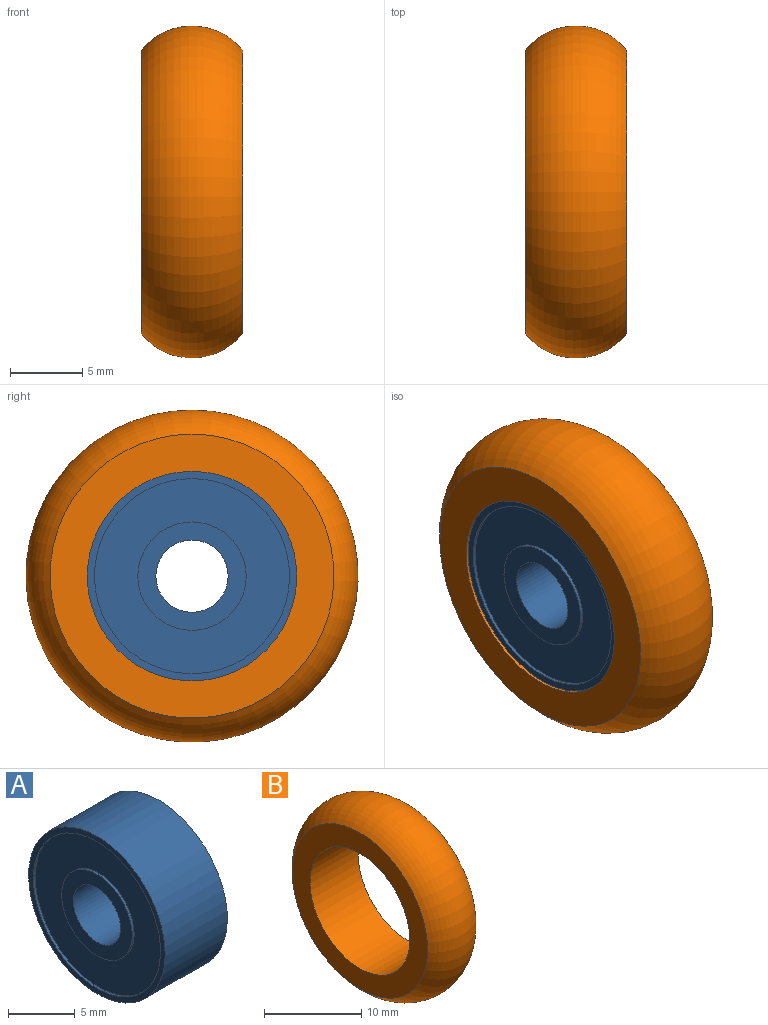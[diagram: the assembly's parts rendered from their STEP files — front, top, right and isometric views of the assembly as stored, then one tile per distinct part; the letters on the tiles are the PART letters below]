
ASSEMBLY  parts=2 mates=2
PART A: 12 faces, bbox 6.6x14.5x14.5 mm
  f0: plane 14.5x14.5mm, normal (-1,0,0), area 22mm2, adj f1,f11
  f1: cylinder r=6.75mm len=13.5mm, axis (-1,0,0), area 8.5mm2, adj f0,f2
  f2: plane 13.5x13.5mm, normal (-1,0,0), area 99mm2, adj f1,f3
  f3: cylinder r=3.75mm len=7.5mm, axis (-1,0,0), area 4.7mm2, adj f2,f4
  f4: plane 7.5x7.5mm, normal (-1,0,0), area 24.5mm2, adj f3,f5
  f5: cylinder r=2.5mm len=6.6mm, axis (-1,0,0), area 103.7mm2, adj f4,f6
  f6: plane 7.5x7.5mm, normal (1,0,0), area 24.5mm2, adj f5,f7
  f7: cylinder r=3.75mm len=7.5mm, axis (-1,0,0), area 4.7mm2, adj f6,f8
  f8: plane 13.5x13.5mm, normal (1,0,0), area 99mm2, adj f7,f9
  f9: cylinder r=6.75mm len=13.5mm, axis (-1,0,0), area 8.5mm2, adj f8,f10
  f10: plane 14.5x14.5mm, normal (1,0,0), area 22mm2, adj f9,f11
  f11: cylinder r=7.25mm len=14.5mm, axis (-1,0,0), area 300.7mm2, adj f0,f10
PART B: 4 faces, bbox 7x24.9x24.9 mm
  f0: plane 19.66x19.66mm, normal (1,0,0), area 138.3mm2, adj f1,f3
  f1: torus R=7mm, axis (-1,0,0), area 550.7mm2, adj f0,f2
  f2: plane 19.66x19.66mm, normal (-1,0,0), area 138.3mm2, adj f1,f3
  f3: cylinder r=7.25mm len=14.5mm, axis (-1,0,0), area 318.9mm2, adj f0,f2
PLACE A t=(8.73,-8.41,6.4)mm
PLACE B t=(8.73,-8.41,6.4)mm
MATE cylindrical A.f1 <-> B.f1  axis (-1,0,0) through (12.03,-8.41,6.4)mm
MATE planar A.f1 <-> B.f1  axis (-1,0,0) through (8.73,-8.41,6.4)mm
